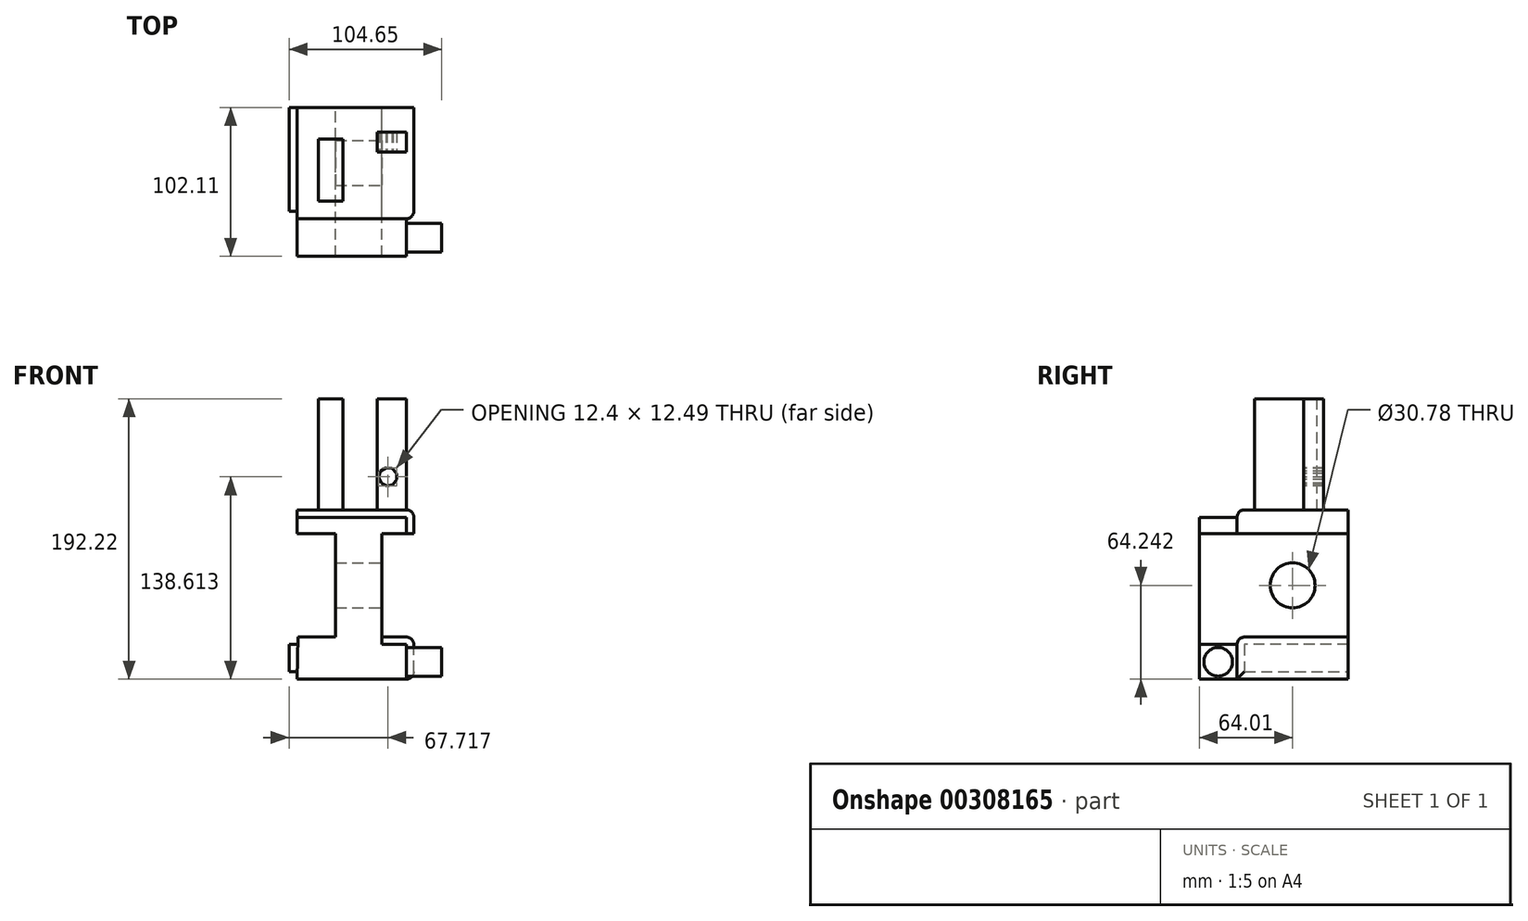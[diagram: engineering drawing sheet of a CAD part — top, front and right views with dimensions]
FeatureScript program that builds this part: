
annotation { "Feature Type Name" : "Feature", "Feature Type Description" : "" }
export const myFeature = defineFeature(function(context is Context, id is Id, definition is map)
    precondition{}
    {
        {
            var Q0;
            Q0=qCreatedBy(makeId("Front.planeOp"),FACE);
            var sketch = newSketch(context, id + "F0", { "sketchPlane" : qUnion([Q0])});
            skLineSegment(sketch, "E0", {"start": v(-41.71, -40.03) * mm, "end": v(38.36, -40.03) * mm});
            skLineSegment(sketch, "E1", {"start": v(38.36, -40.03) * mm, "end": v(38.36, -11.27) * mm});
            skLineSegment(sketch, "E2", {"start": v(38.36, -11.27) * mm, "end": v(16.3, -11.27) * mm});
            skLineSegment(sketch, "E3", {"start": v(16.3, -11.27) * mm, "end": v(16.3, 59.7) * mm});
            skLineSegment(sketch, "E4", {"start": v(16.3, 59.7) * mm, "end": v(38.36, 59.7) * mm});
            skLineSegment(sketch, "E5", {"start": v(38.36, 59.7) * mm, "end": v(38.36, 70.24) * mm});
            skLineSegment(sketch, "E6", {"start": v(38.36, 70.24) * mm, "end": v(38.36, 76) * mm});
            skLineSegment(sketch, "E7", {"start": v(38.36, 76) * mm, "end": v(-41.71, 76) * mm});
            skLineSegment(sketch, "E8", {"start": v(-41.71, 76) * mm, "end": v(-41.71, 59.7) * mm});
            skLineSegment(sketch, "E9", {"start": v(-41.71, 59.7) * mm, "end": v(-15.34, 59.7) * mm});
            skLineSegment(sketch, "E10", {"start": v(-15.34, 59.7) * mm, "end": v(-15.34, -11.27) * mm});
            skLineSegment(sketch, "E11", {"start": v(-15.34, -11.27) * mm, "end": v(-41.23, -11.27) * mm});
            skLineSegment(sketch, "E12", {"start": v(-41.23, -11.27) * mm, "end": v(-41.71, -40.03) * mm});
            skSolve(sketch);
        }
        {
            var Q0;
            Q0=makeQuery(id+"F0.imprint","IMPRINT",FACE,{"disambiguationData":[TD([[makeQuery(id+"F0.imprint","IMPRINT",EDGE,{"derivedFrom":sQuery(id+"F0.wireOp",EDGE,"E0")}),1.0]])]});
            extrude(context, id + "F1", {"entities" : qUnion([Q0]), "depth" : 76.2 * mm});
        }
        {
            var Q0;
            Q0=makeQuery(id+"F1.opExtrude","SWEPT_FACE",FACE,{"disambiguationData":[OSD([sQuery(id+"F0.wireOp",EDGE,"E3")])]});
            var sketch = newSketch(context, id + "F2", { "sketchPlane" : qUnion([Q0])});
            skCircle(sketch, "E13", {"center": v(-38.1, 24.21) * mm, "radius": 15.4 * mm});
            skPoint(sketch, "E13.centerSnap0", {"position": v(-38.1, 59.7) * mm});
            skPoint(sketch, "E13.centerSnap1", {"position": v(-76.2, 24.21) * mm});
            skSolve(sketch);
        }
        {
            var Q0;
            Q0=makeQuery(id+"F2.imprint","IMPRINT",FACE,{"disambiguationData":[TD([[makeQuery(id+"F2.imprint","IMPRINT",EDGE,{"derivedFrom":sQuery(id+"F2.wireOp",EDGE,"E13")}),1.0]])]});
            extrude(context, id + "F3", {"entities" : qUnion([Q0]), "operationType" : NewBodyOperationType.REMOVE, "endBound" : BoundingType.THROUGH_ALL, "oppositeDirection" : true, "depth" : 25.4 * mm});
        }
        {
            var Q0;
            Q0=makeQuery(id+"F1.opExtrude","SWEPT_FACE",FACE,{"disambiguationData":[OSD([sQuery(id+"F0.wireOp",EDGE,"E7")])]});
            var sketch = newSketch(context, id + "F4", { "sketchPlane" : qUnion([Q0])});
            skLineSegment(sketch, "E14.bottom", {"start": v(-27.01, -21.52) * mm, "end": v(-10.17, -21.52) * mm});
            skLineSegment(sketch, "E14.top", {"start": v(-27.01, -32.96) * mm, "end": v(-10.17, -32.96) * mm});
            skLineSegment(sketch, "E14.left", {"start": v(-27.01, -21.52) * mm, "end": v(-27.01, -32.96) * mm});
            skLineSegment(sketch, "E14.right", {"start": v(-10.17, -21.52) * mm, "end": v(-10.17, -32.96) * mm});
            skLineSegment(sketch, "E15.bottom", {"start": v(13.21, -16.8) * mm, "end": v(33.32, -16.8) * mm});
            skLineSegment(sketch, "E15.top", {"start": v(13.21, -30.6) * mm, "end": v(33.32, -30.6) * mm});
            skLineSegment(sketch, "E15.left", {"start": v(13.21, -16.8) * mm, "end": v(13.21, -30.6) * mm});
            skLineSegment(sketch, "E15.right", {"start": v(33.32, -16.8) * mm, "end": v(33.32, -30.6) * mm});
            skSolve(sketch);
        }
        {
            var Q0;
            Q0 = qSketchRegion(id + "F4", true);
            extrude(context, id + "F5", {"entities" : qUnion([Q0]), "operationType" : NewBodyOperationType.ADD, "depth" : 76.2 * mm});
        }
        {
            var Q0;
            Q0=makeQuery(id+"F1.opExtrude","CAP_EDGE",EDGE,{"disambiguationData":[OSD([sQuery(id+"F0.wireOp",EDGE,"E5"),sQuery(id+"F0.wireOp",EDGE,"E6")])],"isStart":false});
            var Q1;
            Q1=makeQuery(id+"F1.opExtrude","SWEPT_EDGE",EDGE,{"disambiguationData":[OSD([sQuery(id+"F0.wireOp",EDGE,"E6"),sQuery(id+"F0.wireOp",EDGE,"E7")])]});
            var Q2;
            Q2=makeQuery(id+"F1.opExtrude","CAP_EDGE",EDGE,{"disambiguationData":[OSD([sQuery(id+"F0.wireOp",EDGE,"E7")])],"isStart":false});
            var Q3;
            Q3=makeQuery(id+"F1.opExtrude","CAP_EDGE",EDGE,{"disambiguationData":[OSD([sQuery(id+"F0.wireOp",EDGE,"E1")])],"isStart":false});
            var Q4;
            Q4=makeQuery(id+"F1.opExtrude","CAP_EDGE",EDGE,{"disambiguationData":[OSD([sQuery(id+"F0.wireOp",EDGE,"E2")])],"isStart":false});
            var Q5;
            Q5=makeQuery(id+"F1.opExtrude","SWEPT_EDGE",EDGE,{"disambiguationData":[OSD([sQuery(id+"F0.wireOp",EDGE,"E1"),sQuery(id+"F0.wireOp",EDGE,"E2")])]});
            var Q6;
            Q6=makeQuery(id+"F1.opExtrude","SWEPT_EDGE",EDGE,{"disambiguationData":[OSD([sQuery(id+"F0.wireOp",EDGE,"E0"),sQuery(id+"F0.wireOp",EDGE,"E1")])]});
            fillet(context, id + "F6", {"entities" : qUnion([Q0, Q1, Q2, Q3, Q4, Q5, Q6]), "radius" : 5.08 * mm, "tangentPropagation" : true, "allowEdgeOverflow" : false});
        }
        {
            var Q0;
            Q0=makeQuery(id+"F5.opExtrude","SWEPT_FACE",FACE,{"disambiguationData":[OSD([sQuery(id+"F4.wireOp",EDGE,"E15.top")])]});
            var sketch = newSketch(context, id + "F7", { "sketchPlane" : qUnion([Q0])});
            skCircle(sketch, "E16.cCircle", {"center": v(20.62, 98.63) * mm, "radius": 5.96 * mm, "construction": true});
            skLineSegment(sketch, "E16.0", {"start": v(19.81, 92.34) * mm, "end": v(15.95, 94.33) * mm});
            skLineSegment(sketch, "E16.1", {"start": v(15.95, 94.33) * mm, "end": v(14.28, 98.34) * mm});
            skLineSegment(sketch, "E16.2", {"start": v(14.28, 98.34) * mm, "end": v(15.57, 102.48) * mm});
            skLineSegment(sketch, "E16.3", {"start": v(15.57, 102.48) * mm, "end": v(19.22, 104.83) * mm});
            skLineSegment(sketch, "E16.4", {"start": v(19.22, 104.83) * mm, "end": v(23.53, 104.27) * mm});
            skLineSegment(sketch, "E16.5", {"start": v(23.53, 104.27) * mm, "end": v(26.47, 101.08) * mm});
            skLineSegment(sketch, "E16.6", {"start": v(26.47, 101.08) * mm, "end": v(26.68, 96.75) * mm});
            skLineSegment(sketch, "E16.7", {"start": v(26.68, 96.75) * mm, "end": v(24.05, 93.3) * mm});
            skLineSegment(sketch, "E16.8", {"start": v(24.05, 93.3) * mm, "end": v(19.81, 92.34) * mm});
            skPoint(sketch, "E16.0.midPoint", {"position": v(17.88, 93.33) * mm});
            skSolve(sketch);
        }
        {
            var Q0;
            Q0=makeQuery(id+"F7.imprint","IMPRINT",FACE,{"disambiguationData":[TD([[makeQuery(id+"F7.imprint","IMPRINT",EDGE,{"derivedFrom":sQuery(id+"F7.wireOp",EDGE,"E16.0")}),-1.0]])]});
            extrude(context, id + "F8", {"entities" : qUnion([Q0]), "operationType" : NewBodyOperationType.REMOVE, "endBound" : BoundingType.THROUGH_ALL, "oppositeDirection" : true, "depth" : 76.2 * mm});
        }
        {
            var Q0;
            Q0=makeQuery(id+"F5.opExtrude","SWEPT_FACE",FACE,{"disambiguationData":[OSD([sQuery(id+"F4.wireOp",EDGE,"E14.top")])]});
            extrude(context, id + "F9", {"entities" : qUnion([Q0]), "operationType" : NewBodyOperationType.ADD, "depth" : 31.24 * mm});
        }
        {
            var Q0;
            Q0=makeQuery(id+"F1.opExtrude","CAP_FACE",FACE,{"disambiguationData":[OSD([sQuery(id+"F0.wireOp",EDGE,"E0"),sQuery(id+"F0.wireOp",EDGE,"E1"),sQuery(id+"F0.wireOp",EDGE,"E2"),sQuery(id+"F0.wireOp",EDGE,"E3"),sQuery(id+"F0.wireOp",EDGE,"E4"),sQuery(id+"F0.wireOp",EDGE,"E5"),sQuery(id+"F0.wireOp",EDGE,"E6"),sQuery(id+"F0.wireOp",EDGE,"E7"),sQuery(id+"F0.wireOp",EDGE,"E8"),sQuery(id+"F0.wireOp",EDGE,"E9"),sQuery(id+"F0.wireOp",EDGE,"E10"),sQuery(id+"F0.wireOp",EDGE,"E11"),sQuery(id+"F0.wireOp",EDGE,"E12")])],"isStart":false});
            extrude(context, id + "F10", {"entities" : qUnion([Q0]), "operationType" : NewBodyOperationType.ADD, "depth" : 25.9 * mm});
        }
        {
            var Q0;
            Q0=makeQuery(id+"F1.opExtrude","SWEPT_FACE",FACE,{"disambiguationData":[OSD([sQuery(id+"F0.wireOp",EDGE,"E1")])]});
            extrude(context, id + "F11", {"entities" : qUnion([Q0]), "operationType" : NewBodyOperationType.ADD, "oppositeDirection" : true, "depth" : 85.6 * mm});
        }
        {
            var Q0;
            {var subQ0=sQuery(id+"F0.wireOp",EDGE,"E12");var subQ1=sQuery(id+"F0.wireOp",EDGE,"E11");var subQ2=sQuery(id+"F0.wireOp",EDGE,"E10");var subQ3=sQuery(id+"F0.wireOp",EDGE,"E9");var subQ4=sQuery(id+"F0.wireOp",EDGE,"E8");var subQ5=sQuery(id+"F0.wireOp",EDGE,"E7");var subQ6=sQuery(id+"F0.wireOp",EDGE,"E6");var subQ7=sQuery(id+"F0.wireOp",EDGE,"E5");var subQ8=sQuery(id+"F0.wireOp",EDGE,"E4");var subQ9=sQuery(id+"F0.wireOp",EDGE,"E3");var subQ10=sQuery(id+"F0.wireOp",EDGE,"E2");var subQ11=sQuery(id+"F0.wireOp",EDGE,"E1");var subQ12=sQuery(id+"F0.wireOp",EDGE,"E0");Q0=makeQuery(id+"F10.opExtrude","SWEPT_FACE",FACE,{"disambiguationData":[OSD([subQ12,subQ11,subQ10,subQ9,subQ8,subQ7,subQ6,subQ5,subQ4,subQ3,subQ2,subQ1,subQ0]),TDD([makeQuery(id+"F6.opFillet","BLEND_EDGE",EDGE,{"blendedFrom":[makeQuery(id+"F1.opExtrude","CAP_EDGE",EDGE,{"disambiguationData":[OSD([subQ11])],"isStart":false}),makeQuery(id+"F1.opExtrude","CAP_FACE",FACE,{"disambiguationData":[OSD([subQ12,subQ11,subQ10,subQ9,subQ8,subQ7,subQ6,subQ5,subQ4,subQ3,subQ2,subQ1,subQ0])],"isStart":false})],"blendedInto":[makeQuery(id+"F1.opExtrude","CAP_FACE",FACE,{"disambiguationData":[OSD([subQ12,subQ11,subQ10,subQ9,subQ8,subQ7,subQ6,subQ5,subQ4,subQ3,subQ2,subQ1,subQ0])],"isStart":false})]})])]});}
            var sketch = newSketch(context, id + "F12", { "sketchPlane" : qUnion([Q0])});
            skCircle(sketch, "E17", {"center": v(-89.15, -28.2) * mm, "radius": 9.81 * mm});
            skPoint(sketch, "E17.centerSnap0", {"position": v(-102.1, -28.2) * mm});
            skPoint(sketch, "E17.centerSnap1", {"position": v(-89.15, -16.35) * mm});
            skSolve(sketch);
        }
        {
            var Q0;
            Q0=makeQuery(id+"F12.imprint","IMPRINT",FACE,{"disambiguationData":[TD([[makeQuery(id+"F12.imprint","IMPRINT",EDGE,{"derivedFrom":sQuery(id+"F12.wireOp",EDGE,"E17")}),1.0]])]});
            extrude(context, id + "F13", {"entities" : qUnion([Q0]), "operationType" : NewBodyOperationType.ADD, "depth" : 24.13 * mm});
        }
    });
